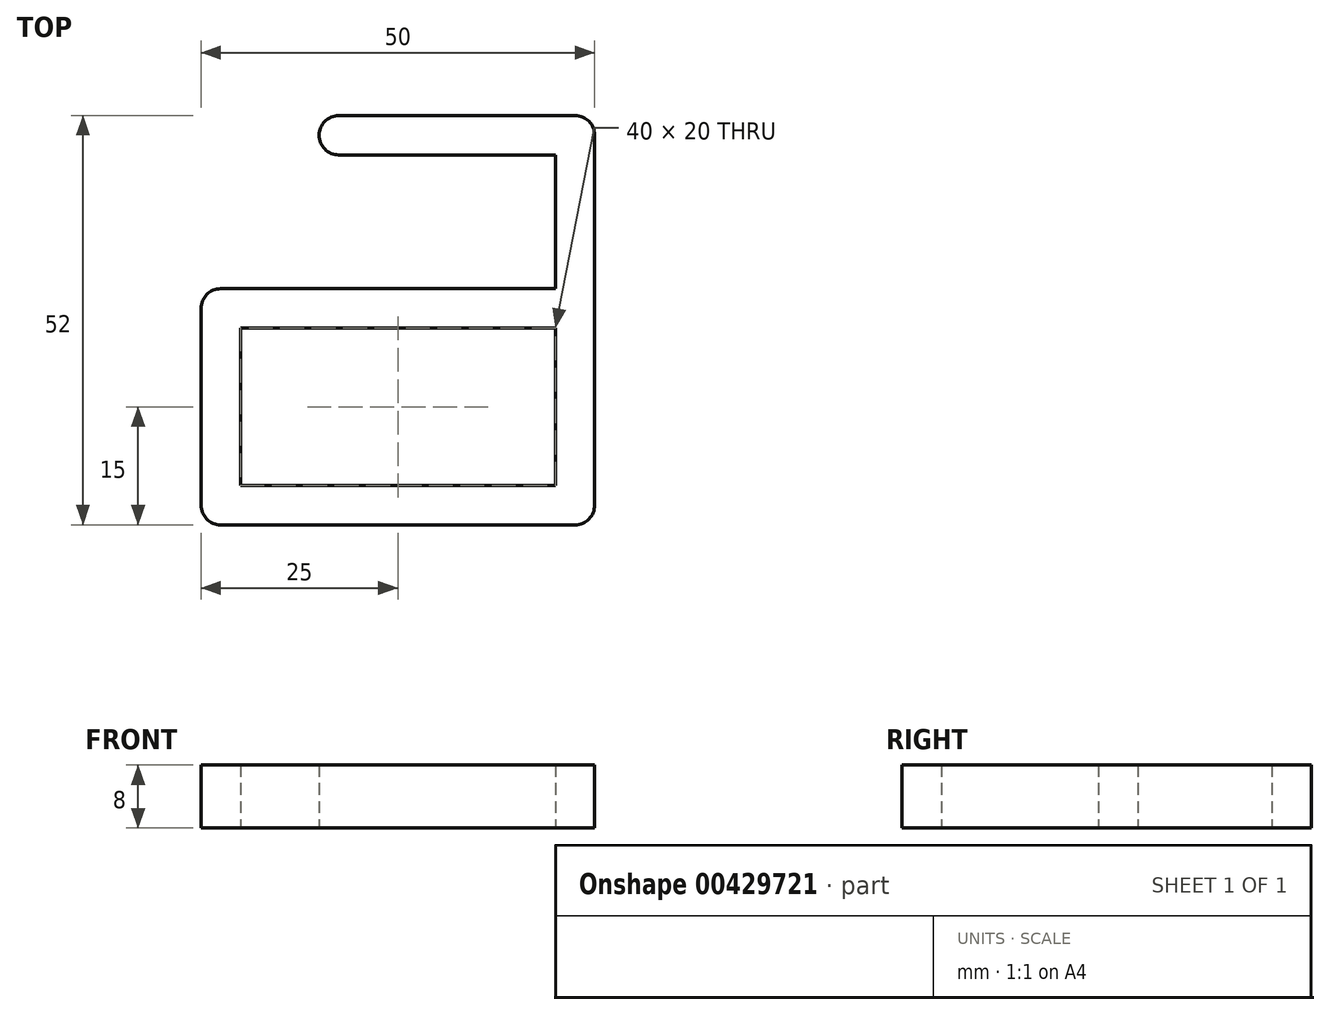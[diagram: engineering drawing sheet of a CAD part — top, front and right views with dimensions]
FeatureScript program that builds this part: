
annotation { "Feature Type Name" : "Feature", "Feature Type Description" : "" }
export const myFeature = defineFeature(function(context is Context, id is Id, definition is map)
    precondition{}
    {
        {
            var Q0;
            Q0=qCreatedBy(makeId("Top.planeOp"),FACE);
            var sketch = newSketch(context, id + "F0", { "sketchPlane" : qUnion([Q0])});
            skLineSegment(sketch, "E0.bottom", {"start": v(0, 0) * mm, "end": v(40, 0) * mm});
            skLineSegment(sketch, "E0.top", {"start": v(0, 20) * mm, "end": v(40, 20) * mm});
            skLineSegment(sketch, "E0.left", {"start": v(0, 0) * mm, "end": v(0, 20) * mm});
            skLineSegment(sketch, "E0.right", {"start": v(40, 0) * mm, "end": v(40, 20) * mm});
            skLineSegment(sketch, "E1.0", {"start": v(-2.5, 25) * mm, "end": v(40, 25) * mm});
            skLineSegment(sketch, "E1.1", {"start": v(-5, -2.5) * mm, "end": v(-5, 22.5) * mm});
            skLineSegment(sketch, "E1.2", {"start": v(-2.5, -5) * mm, "end": v(42.5, -5) * mm});
            skLineSegment(sketch, "E1.3", {"start": v(45, -2.5) * mm, "end": v(45, 25) * mm});
            skLineSegment(sketch, "E2", {"start": v(40, 25) * mm, "end": v(40, 42) * mm});
            skLineSegment(sketch, "E3", {"start": v(40, 42) * mm, "end": v(12.5, 42) * mm});
            skLineSegment(sketch, "E4", {"start": v(10, 44.5) * mm, "end": v(10, 44.5) * mm});
            skLineSegment(sketch, "E5", {"start": v(12.5, 47) * mm, "end": v(42.5, 47) * mm});
            skLineSegment(sketch, "E6", {"start": v(45, 44.5) * mm, "end": v(45, 25) * mm});
            skPoint(sketch, "E7.visualSharp", {"position": v(10, 47) * mm});
            skArc(sketch, "E7.filletArc", {"start": v(12.5, 47) * mm, "mid": v(10.73, 46.27) * mm, "end": v(10, 44.5) * mm});
            skPoint(sketch, "E8.visualSharp", {"position": v(10, 42) * mm});
            skArc(sketch, "E8.filletArc", {"start": v(10, 44.5) * mm, "mid": v(10.73, 42.73) * mm, "end": v(12.5, 42) * mm});
            skPoint(sketch, "E9.visualSharp", {"position": v(-5, 25) * mm});
            skArc(sketch, "E9.filletArc", {"start": v(-2.5, 25) * mm, "mid": v(-4.27, 24.27) * mm, "end": v(-5, 22.5) * mm});
            skPoint(sketch, "E10.visualSharp", {"position": v(-5, -5) * mm});
            skArc(sketch, "E10.filletArc", {"start": v(-5, -2.5) * mm, "mid": v(-4.27, -4.27) * mm, "end": v(-2.5, -5) * mm});
            skPoint(sketch, "E11.visualSharp", {"position": v(45, -5) * mm});
            skArc(sketch, "E11.filletArc", {"start": v(42.5, -5) * mm, "mid": v(44.27, -4.27) * mm, "end": v(45, -2.5) * mm});
            skPoint(sketch, "E12.visualSharp", {"position": v(45, 47) * mm});
            skArc(sketch, "E12.filletArc", {"start": v(45, 44.5) * mm, "mid": v(44.27, 46.27) * mm, "end": v(42.5, 47) * mm});
            skSolve(sketch);
        }
        {
            var Q0;
            Q0=makeQuery(id+"F0.imprint","IMPRINT",FACE,{"disambiguationData":[TD([[makeQuery(id+"F0.imprint","IMPRINT",EDGE,{"derivedFrom":sQuery(id+"F0.wireOp",EDGE,"E0.bottom")}),-1.0]])]});
            extrude(context, id + "F1", {"entities" : qUnion([Q0]), "depth" : 8 * mm});
        }
    });
